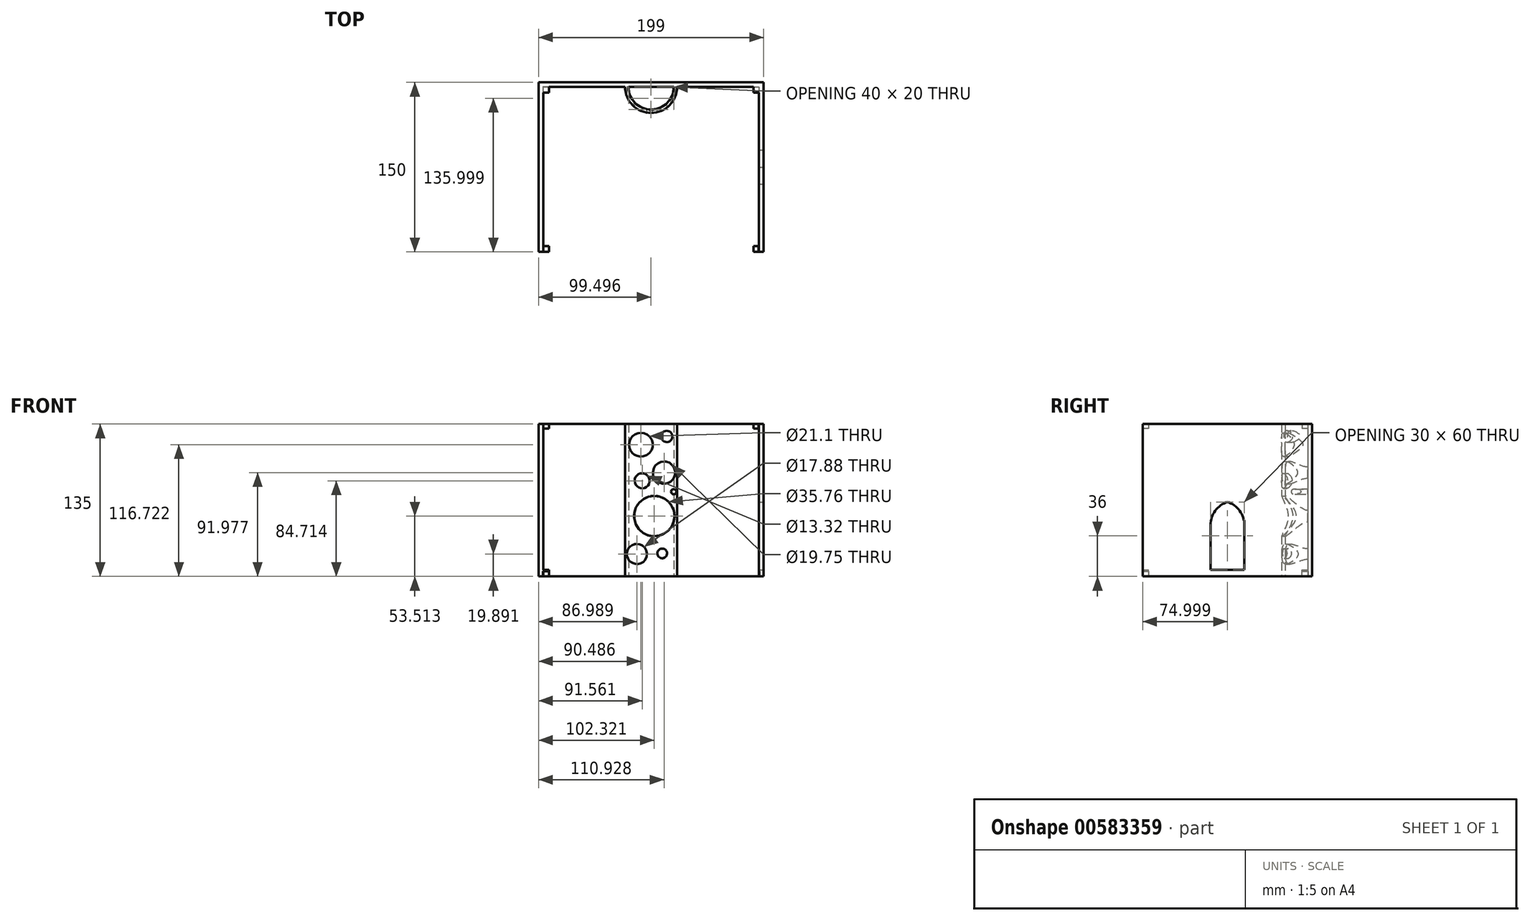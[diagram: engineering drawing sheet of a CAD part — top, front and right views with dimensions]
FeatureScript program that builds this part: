
annotation { "Feature Type Name" : "Feature", "Feature Type Description" : "" }
export const myFeature = defineFeature(function(context is Context, id is Id, definition is map)
    precondition{}
    {
        {
            var Q0;
            Q0=qCreatedBy(makeId("Top.planeOp"),FACE);
            var sketch = newSketch(context, id + "F0", { "sketchPlane" : qUnion([Q0])});
            skLineSegment(sketch, "E0.bottom", {"start": v(-101.05, 94.09) * mm, "end": v(97.95, 94.09) * mm});
            skLineSegment(sketch, "E0.top", {"start": v(-101.05, -55.91) * mm, "end": v(97.95, -55.91) * mm});
            skLineSegment(sketch, "E0.left", {"start": v(-101.05, 94.09) * mm, "end": v(-101.05, -55.91) * mm});
            skLineSegment(sketch, "E0.right", {"start": v(97.95, 94.09) * mm, "end": v(97.95, -55.91) * mm});
            skLineSegment(sketch, "E1", {"start": v(-97.05, -55.91) * mm, "end": v(-97.05, 90.09) * mm});
            skLineSegment(sketch, "E2", {"start": v(-97.05, 90.09) * mm, "end": v(-24.55, 90.09) * mm});
            skLineSegment(sketch, "E3", {"start": v(93.95, 90.09) * mm, "end": v(93.95, -55.91) * mm});
            skLineSegment(sketch, "E4.bottom", {"start": v(-97.05, 90.09) * mm, "end": v(-92.05, 90.09) * mm});
            skLineSegment(sketch, "E4.left", {"start": v(-97.05, 90.09) * mm, "end": v(-97.05, 85.09) * mm});
            skLineSegment(sketch, "E5.bottom", {"start": v(93.95, 90.09) * mm, "end": v(88.95, 90.09) * mm});
            skLineSegment(sketch, "E5.left", {"start": v(93.95, 90.09) * mm, "end": v(93.95, 85.09) * mm});
            skLineSegment(sketch, "E6.bottom", {"start": v(93.95, -55.91) * mm, "end": v(88.95, -55.91) * mm});
            skLineSegment(sketch, "E6.left", {"start": v(93.95, -55.91) * mm, "end": v(93.95, -50.91) * mm});
            skLineSegment(sketch, "E7.bottom", {"start": v(-97.05, -55.91) * mm, "end": v(-92.05, -55.91) * mm});
            skLineSegment(sketch, "E7.left", {"start": v(-97.05, -55.91) * mm, "end": v(-97.05, -50.91) * mm});
            skArc(sketch, "E8", {"start": v(-21.55, 90.09) * mm, "mid": v(-1.55, 70.09) * mm, "end": v(18.45, 90.09) * mm});
            skArc(sketch, "E9", {"start": v(-24.55, 90.09) * mm, "mid": v(-1.55, 67.09) * mm, "end": v(21.45, 90.09) * mm});
            skLineSegment(sketch, "E10.trimOffspring", {"start": v(-21.55, 90.09) * mm, "end": v(18.45, 90.09) * mm});
            skLineSegment(sketch, "E11.trimOffspring", {"start": v(21.45, 90.09) * mm, "end": v(93.95, 90.09) * mm});
            skLineSegment(sketch, "E12", {"start": v(-97.05, 85.09) * mm, "end": v(-92.05, 85.09) * mm});
            skLineSegment(sketch, "E13", {"start": v(-92.05, 85.09) * mm, "end": v(-92.05, 90.09) * mm});
            skLineSegment(sketch, "E14", {"start": v(-97.05, -50.91) * mm, "end": v(-92.05, -50.91) * mm});
            skLineSegment(sketch, "E15", {"start": v(-92.05, -50.91) * mm, "end": v(-92.05, -55.91) * mm});
            skLineSegment(sketch, "E16", {"start": v(88.95, -55.91) * mm, "end": v(88.95, -50.91) * mm});
            skLineSegment(sketch, "E17", {"start": v(88.95, -50.91) * mm, "end": v(93.95, -50.91) * mm});
            skLineSegment(sketch, "E18", {"start": v(88.95, 90.09) * mm, "end": v(88.95, 85.09) * mm});
            skLineSegment(sketch, "E19", {"start": v(88.95, 85.09) * mm, "end": v(93.95, 85.09) * mm});
            skSolve(sketch);
        }
        {
            var Q0;
            Q0=makeQuery(id+"F0.imprint","IMPRINT",FACE,{"disambiguationData":[TD([[makeQuery(id+"F0.imprint","IMPRINT",EDGE,{"derivedFrom":sQuery(id+"F0.wireOp",EDGE,"E0.bottom")}),-1.0]])]});
            var Q1;
            Q1=makeQuery(id+"F0.imprint","IMPRINT",FACE,{"disambiguationData":[TD([[makeQuery(id+"F0.imprint","IMPRINT",EDGE,{"derivedFrom":sQuery(id+"F0.wireOp",EDGE,"E7.bottom")}),1.0]])]});
            var Q2;
            Q2=makeQuery(id+"F0.imprint","IMPRINT",FACE,{"disambiguationData":[TD([[makeQuery(id+"F0.imprint","IMPRINT",EDGE,{"derivedFrom":sQuery(id+"F0.wireOp",EDGE,"E6.bottom")}),-1.0]])]});
            var Q3;
            {var subQ0=sQuery(id+"F0.wireOp",EDGE,"E5.left");Q3=makeQuery(id+"F0.imprint","IMPRINT",FACE,{"disambiguationData":[TD([[makeQuery(id+"F0.imprint","IMPRINT",EDGE,{"derivedFrom":subQ0}),-1.0]])]});}
            var Q4;
            Q4=makeQuery(id+"F0.imprint","IMPRINT",FACE,{"disambiguationData":[TD([[makeQuery(id+"F0.imprint","IMPRINT",EDGE,{"derivedFrom":sQuery(id+"F0.wireOp",EDGE,"E4.bottom")}),-1.0]])]});
            extrude(context, id + "F1", {"entities" : qUnion([Q0, Q1, Q2, Q3, Q4]), "depth" : 125 * mm, "offsetDistance" : 25 * mm});
        }
        {
            var Q0;
            Q0=makeQuery(id+"F0.imprint","IMPRINT",FACE,{"disambiguationData":[TD([[makeQuery(id+"F0.imprint","IMPRINT",EDGE,{"derivedFrom":sQuery(id+"F0.wireOp",EDGE,"E0.bottom")}),-1.0]])]});
            var Q1;
            Q1=makeQuery(id+"F0.imprint","IMPRINT",FACE,{"disambiguationData":[TD([[makeQuery(id+"F0.imprint","IMPRINT",EDGE,{"derivedFrom":sQuery(id+"F0.wireOp",EDGE,"E6.bottom")}),-1.0]])]});
            var Q2;
            Q2=makeQuery(id+"F0.imprint","IMPRINT",FACE,{"disambiguationData":[TD([[makeQuery(id+"F0.imprint","IMPRINT",EDGE,{"derivedFrom":sQuery(id+"F0.wireOp",EDGE,"E7.bottom")}),1.0]])]});
            var Q3;
            Q3=makeQuery(id+"F0.imprint","IMPRINT",FACE,{"disambiguationData":[TD([[makeQuery(id+"F0.imprint","IMPRINT",EDGE,{"derivedFrom":sQuery(id+"F0.wireOp",EDGE,"E4.bottom")}),-1.0]])]});
            var Q4;
            {var subQ0=sQuery(id+"F0.wireOp",EDGE,"E5.left");Q4=makeQuery(id+"F0.imprint","IMPRINT",FACE,{"disambiguationData":[TD([[makeQuery(id+"F0.imprint","IMPRINT",EDGE,{"derivedFrom":subQ0}),-1.0]])]});}
            var Q5;
            Q5=makeQuery(id+"F0.imprint","IMPRINT",FACE,{"disambiguationData":[TD([[makeQuery(id+"F0.imprint","IMPRINT",EDGE,{"derivedFrom":sQuery(id+"F0.wireOp",EDGE,"E1")}),-1.0]])]});
            extrude(context, id + "F2", {"entities" : qUnion([Q0, Q1, Q2, Q3, Q4, Q5]), "operationType" : NewBodyOperationType.ADD, "oppositeDirection" : true, "depth" : 6 * mm, "offsetDistance" : 25 * mm});
        }
        {
            var Q0;
            Q0=makeQuery(id+"F1.opExtrude","CAP_FACE",FACE,{"disambiguationData":[OSD([sQuery(id+"F0.wireOp",EDGE,"E0.bottom"),sQuery(id+"F0.wireOp",EDGE,"E0.top"),sQuery(id+"F0.wireOp",EDGE,"E0.left"),sQuery(id+"F0.wireOp",EDGE,"E0.right"),sQuery(id+"F0.wireOp",EDGE,"E1"),sQuery(id+"F0.wireOp",EDGE,"E2"),sQuery(id+"F0.wireOp",EDGE,"E3"),sQuery(id+"F0.wireOp",EDGE,"E6.bottom"),sQuery(id+"F0.wireOp",EDGE,"E7.bottom"),sQuery(id+"F0.wireOp",EDGE,"E8"),sQuery(id+"F0.wireOp",EDGE,"E9"),sQuery(id+"F0.wireOp",EDGE,"E10.trimOffspring"),sQuery(id+"F0.wireOp",EDGE,"E11.trimOffspring"),sQuery(id+"F0.wireOp",EDGE,"E12"),sQuery(id+"F0.wireOp",EDGE,"E13"),sQuery(id+"F0.wireOp",EDGE,"E14"),sQuery(id+"F0.wireOp",EDGE,"E15"),sQuery(id+"F0.wireOp",EDGE,"E16"),sQuery(id+"F0.wireOp",EDGE,"E17"),sQuery(id+"F0.wireOp",EDGE,"E18"),sQuery(id+"F0.wireOp",EDGE,"E19")])],"isStart":false});
            var sketch = newSketch(context, id + "F3", { "sketchPlane" : qUnion([Q0])});
            skLineSegment(sketch, "E20", {"start": v(-92.05, 90.09) * mm, "end": v(-97.05, 90.09) * mm});
            skLineSegment(sketch, "E21", {"start": v(-97.05, 90.09) * mm, "end": v(-97.05, 85.09) * mm});
            skLineSegment(sketch, "E22", {"start": v(-97.05, 85.09) * mm, "end": v(-92.05, 85.09) * mm});
            skLineSegment(sketch, "E23", {"start": v(-92.05, 85.09) * mm, "end": v(-92.05, 90.09) * mm});
            skLineSegment(sketch, "E24", {"start": v(-97.05, -50.91) * mm, "end": v(-97.05, -55.91) * mm});
            skPoint(sketch, "E24.endSnap0", {"position": v(-96.55, -55.91) * mm});
            skLineSegment(sketch, "E25", {"start": v(-97.05, -55.91) * mm, "end": v(-92.05, -55.91) * mm});
            skLineSegment(sketch, "E26", {"start": v(-97.05, -50.91) * mm, "end": v(-92.05, -50.91) * mm});
            skLineSegment(sketch, "E27.bottom", {"start": v(88.95, -50.91) * mm, "end": v(93.45, -50.91) * mm});
            skLineSegment(sketch, "E27.top", {"start": v(88.95, -55.91) * mm, "end": v(93.45, -55.91) * mm});
            skLineSegment(sketch, "E27.left", {"start": v(88.95, -50.91) * mm, "end": v(88.95, -55.91) * mm});
            skLineSegment(sketch, "E27.right", {"start": v(93.45, -50.91) * mm, "end": v(93.45, -55.91) * mm});
            skPoint(sketch, "E28.oppositeSnap0", {"position": v(93.95, 17.09) * mm});
            skLineSegment(sketch, "E28.bottom", {"start": v(88.95, 85.09) * mm, "end": v(93.95, 85.09) * mm});
            skLineSegment(sketch, "E28.top", {"start": v(88.95, 90.09) * mm, "end": v(93.95, 90.09) * mm});
            skLineSegment(sketch, "E28.left", {"start": v(88.95, 85.09) * mm, "end": v(88.95, 90.09) * mm});
            skLineSegment(sketch, "E28.right", {"start": v(93.95, 85.09) * mm, "end": v(93.95, 90.09) * mm});
            skSolve(sketch);
        }
        {
            var Q0;
            Q0 = qSketchRegion(id + "F3", true);
            var Q1;
            Q1=makeQuery(id+"F3.imprint","IMPRINT",FACE,{"disambiguationData":[TD([[makeQuery(id+"F3.imprint","IMPRINT",EDGE,{"derivedFrom":sQuery(id+"F3.wireOp",EDGE,"E24")}),1.0]])]});
            extrude(context, id + "F4", {"entities" : qUnion([Q0, Q1]), "operationType" : NewBodyOperationType.ADD, "depth" : 4 * mm, "offsetDistance" : 25 * mm});
        }
        {
            var Q0;
            Q0=makeQuery(id+"F2.opExtrude","CAP_FACE",FACE,{"disambiguationData":[OSD([sQuery(id+"F0.wireOp",EDGE,"E0.bottom"),sQuery(id+"F0.wireOp",EDGE,"E0.top"),sQuery(id+"F0.wireOp",EDGE,"E0.left"),sQuery(id+"F0.wireOp",EDGE,"E0.right"),sQuery(id+"F0.wireOp",EDGE,"E6.bottom"),sQuery(id+"F0.wireOp",EDGE,"E7.bottom"),sQuery(id+"F0.wireOp",EDGE,"E8"),sQuery(id+"F0.wireOp",EDGE,"E10.trimOffspring")])],"isStart":false});
            var sketch = newSketch(context, id + "F5", { "sketchPlane" : qUnion([Q0])});
            skLineSegment(sketch, "E29.bottom", {"start": v(-97.3, 55.91) * mm, "end": v(-91.8, 55.91) * mm});
            skLineSegment(sketch, "E29.top", {"start": v(-97.3, 50.41) * mm, "end": v(-91.8, 50.41) * mm});
            skLineSegment(sketch, "E29.left", {"start": v(-97.3, 55.91) * mm, "end": v(-97.3, 50.41) * mm});
            skLineSegment(sketch, "E29.right", {"start": v(-91.8, 55.91) * mm, "end": v(-91.8, 50.41) * mm});
            skLineSegment(sketch, "E30.bottom", {"start": v(-97.3, -90.34) * mm, "end": v(-91.8, -90.34) * mm});
            skLineSegment(sketch, "E30.top", {"start": v(-97.3, -84.84) * mm, "end": v(-91.8, -84.84) * mm});
            skLineSegment(sketch, "E30.left", {"start": v(-97.3, -90.34) * mm, "end": v(-97.3, -84.84) * mm});
            skLineSegment(sketch, "E30.right", {"start": v(-91.8, -90.34) * mm, "end": v(-91.8, -84.84) * mm});
            skLineSegment(sketch, "E31.bottom", {"start": v(88.7, -84.84) * mm, "end": v(94.2, -84.84) * mm});
            skLineSegment(sketch, "E31.top", {"start": v(88.7, -90.34) * mm, "end": v(94.2, -90.34) * mm});
            skLineSegment(sketch, "E31.left", {"start": v(88.7, -84.84) * mm, "end": v(88.7, -90.34) * mm});
            skLineSegment(sketch, "E31.right", {"start": v(94.2, -84.84) * mm, "end": v(94.2, -90.34) * mm});
            skLineSegment(sketch, "E32.bottom", {"start": v(88.7, 50.41) * mm, "end": v(94.2, 50.41) * mm});
            skLineSegment(sketch, "E32.top", {"start": v(88.7, 55.91) * mm, "end": v(94.2, 55.91) * mm});
            skLineSegment(sketch, "E32.left", {"start": v(88.7, 50.41) * mm, "end": v(88.7, 55.91) * mm});
            skLineSegment(sketch, "E32.right", {"start": v(94.2, 50.41) * mm, "end": v(94.2, 55.91) * mm});
            skCircle(sketch, "E33", {"center": v(-67.05, -60.09) * mm, "radius": 20 * mm});
            skSolve(sketch);
        }
        {
            var Q0;
            Q0=makeQuery(id+"F5.imprint","IMPRINT",FACE,{"disambiguationData":[TD([[makeQuery(id+"F5.imprint","IMPRINT",EDGE,{"derivedFrom":sQuery(id+"F5.wireOp",EDGE,"E29.bottom")}),-1.0]])]});
            var Q1;
            Q1=makeQuery(id+"F5.imprint","IMPRINT",FACE,{"disambiguationData":[TD([[makeQuery(id+"F5.imprint","IMPRINT",EDGE,{"derivedFrom":sQuery(id+"F5.wireOp",EDGE,"E30.bottom")}),1.0]])]});
            var Q2;
            Q2=makeQuery(id+"F5.imprint","IMPRINT",FACE,{"disambiguationData":[TD([[makeQuery(id+"F5.imprint","IMPRINT",EDGE,{"derivedFrom":sQuery(id+"F5.wireOp",EDGE,"E32.bottom")}),1.0]])]});
            var Q3;
            Q3=makeQuery(id+"F5.imprint","IMPRINT",FACE,{"disambiguationData":[TD([[makeQuery(id+"F5.imprint","IMPRINT",EDGE,{"derivedFrom":sQuery(id+"F5.wireOp",EDGE,"E31.bottom")}),-1.0]])]});
            extrude(context, id + "F6", {"entities" : qUnion([Q0, Q1, Q2, Q3]), "operationType" : NewBodyOperationType.REMOVE, "oppositeDirection" : true, "depth" : 4.5 * mm, "offsetDistance" : 25 * mm});
        }
        {
            var Q0;
            Q0=makeQuery(id+"F5.imprint","IMPRINT",FACE,{"disambiguationData":[TD([[makeQuery(id+"F5.imprint","IMPRINT",EDGE,{"derivedFrom":sQuery(id+"F5.wireOp",EDGE,"E33")}),1.0]])]});
            extrude(context, id + "F7", {"entities" : qUnion([Q0]), "operationType" : NewBodyOperationType.REMOVE, "oppositeDirection" : true, "depth" : 25 * mm, "offsetDistance" : 25 * mm});
        }
        {
            var Q0;
            {var subQ0=sQuery(id+"F0.wireOp",EDGE,"E0.right");Q0=makeQuery(id+"F2.boolean.opBoolean","MERGE",FACE,{"derivedFrom":[makeQuery(id+"F1.opExtrude","SWEPT_FACE",FACE,{"disambiguationData":[OSD([subQ0])]}),makeQuery(id+"F2.opExtrude","SWEPT_FACE",FACE,{"disambiguationData":[OSD([subQ0])]})]});}
            var sketch = newSketch(context, id + "F8", { "sketchPlane" : qUnion([Q0])});
            skLineSegment(sketch, "E34", {"start": v(4.09, -6) * mm, "end": v(4.09, 39.46) * mm});
            skLineSegment(sketch, "E35", {"start": v(34.09, -6) * mm, "end": v(34.09, 39.46) * mm});
            skLineSegment(sketch, "E36", {"start": v(4.09, 0) * mm, "end": v(34.09, 0) * mm});
            skArc(sketch, "E37", {"start": v(19.09, 60) * mm, "mid": v(8.24, 52.18) * mm, "end": v(4.09, 39.46) * mm});
            skArc(sketch, "E38", {"start": v(34.09, 39.46) * mm, "mid": v(29.94, 52.18) * mm, "end": v(19.09, 60) * mm});
            skLineSegment(sketch, "E39", {"start": v(19.09, 60) * mm, "end": v(19.09, -6) * mm});
            skSolve(sketch);
        }
        {
            var Q0;
            Q0 = qSketchRegion(id + "F8", true);
            extrude(context, id + "F9", {"entities" : qUnion([Q0]), "operationType" : NewBodyOperationType.REMOVE, "oppositeDirection" : true, "depth" : 25 * mm, "offsetDistance" : 25 * mm});
        }
        {
            var Q0;
            {var subQ0=sQuery(id+"F0.wireOp",EDGE,"E10.trimOffspring");Q0=makeQuery(id+"F2.boolean.opBoolean","MERGE",FACE,{"derivedFrom":[makeQuery(id+"F1.opExtrude","SWEPT_FACE",FACE,{"disambiguationData":[OSD([subQ0])]}),makeQuery(id+"F2.opExtrude","SWEPT_FACE",FACE,{"disambiguationData":[OSD([subQ0])]})]});}
            var sketch = newSketch(context, id + "F10", { "sketchPlane" : qUnion([Q0])});
            skCircle(sketch, "E40", {"center": v(-10.56, 110.72) * mm, "radius": 10.55 * mm});
            skCircle(sketch, "E41", {"center": v(12.3, 117.98) * mm, "radius": 5.05 * mm});
            skCircle(sketch, "E42", {"center": v(9.88, 85.98) * mm, "radius": 9.88 * mm});
            skCircle(sketch, "E43", {"center": v(1.27, 47.51) * mm, "radius": 17.88 * mm});
            skCircle(sketch, "E44", {"center": v(-9.49, 78.71) * mm, "radius": 6.66 * mm});
            skCircle(sketch, "E45", {"center": v(18.45, 69.03) * mm, "radius": 2.28 * mm});
            skCircle(sketch, "E46", {"center": v(-14.06, 13.9) * mm, "radius": 8.94 * mm});
            skCircle(sketch, "E47", {"center": v(8.26, 14.43) * mm, "radius": 4.31 * mm});
            skSolve(sketch);
        }
        {
            var Q0;
            Q0 = qSketchRegion(id + "F10", true);
            extrude(context, id + "F11", {"entities" : qUnion([Q0]), "operationType" : NewBodyOperationType.REMOVE, "depth" : 97.8 * mm, "offsetDistance" : 25 * mm});
        }
    });
